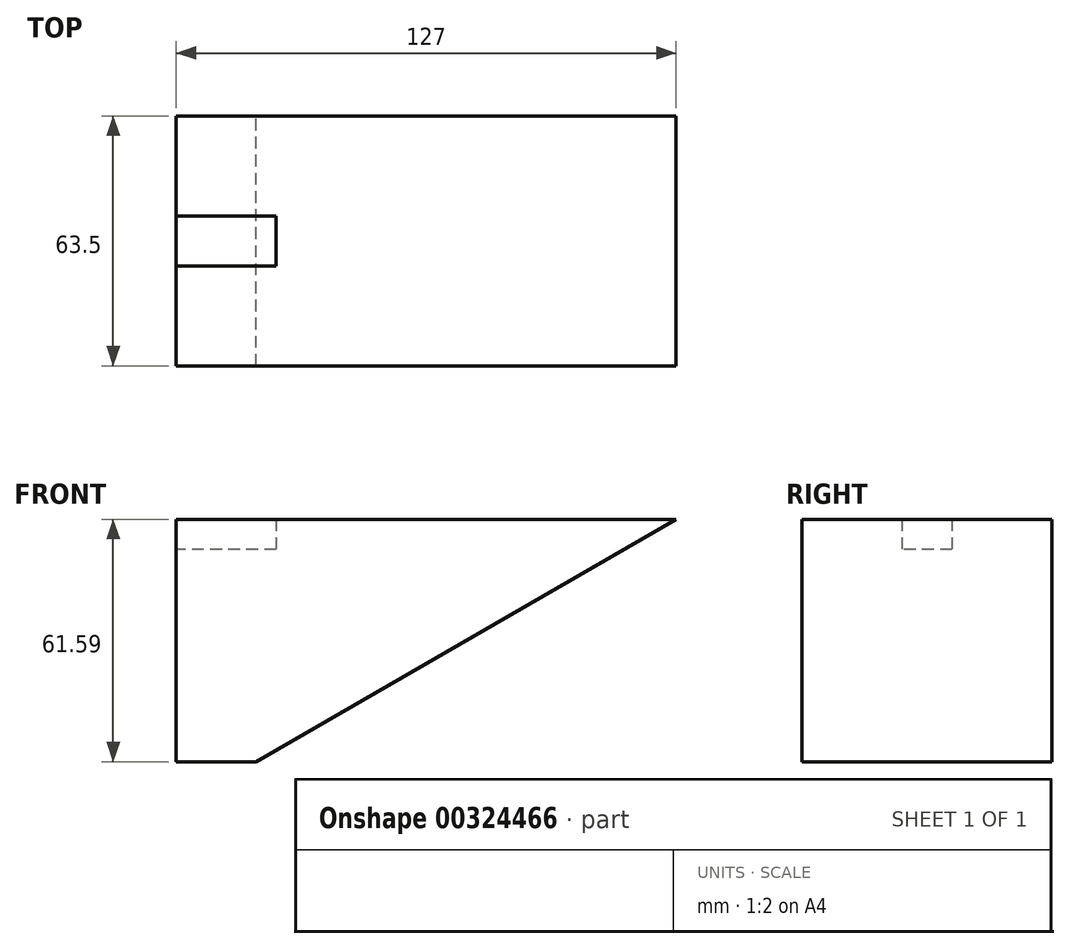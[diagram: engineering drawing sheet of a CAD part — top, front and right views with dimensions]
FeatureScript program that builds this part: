
annotation { "Feature Type Name" : "Feature", "Feature Type Description" : "" }
export const myFeature = defineFeature(function(context is Context, id is Id, definition is map)
    precondition{}
    {
        {
            var Q0;
            Q0=qCreatedBy(makeId("Front.planeOp"),FACE);
            var sketch = newSketch(context, id + "F0", { "sketchPlane" : qUnion([Q0])});
            skLineSegment(sketch, "E0", {"start": v(0, 0) * mm, "end": v(20.32, 0) * mm});
            skLineSegment(sketch, "E1", {"start": v(0, 0) * mm, "end": v(0, 61.6) * mm});
            skLineSegment(sketch, "E2", {"start": v(127, 61.6) * mm, "end": v(20.32, 0) * mm});
            skLineSegment(sketch, "E3", {"start": v(62.26, 61.6) * mm, "end": v(127, 61.6) * mm});
            skLineSegment(sketch, "E4", {"start": v(0, 61.6) * mm, "end": v(127, 61.6) * mm});
            skSolve(sketch);
        }
        {
            var Q0;
            Q0 = qSketchRegion(id + "F0", true);
            extrude(context, id + "F1", {"entities" : qUnion([Q0]), "depth" : 63.5 * mm});
        }
        {
            var Q0;
            Q0=makeQuery(id+"F1.opExtrude","SWEPT_FACE",FACE,{"disambiguationData":[OSD([sQuery(id+"F0.wireOp",EDGE,"E1")])]});
            var sketch = newSketch(context, id + "F2", { "sketchPlane" : qUnion([Q0])});
            skLineSegment(sketch, "E5.bottom", {"start": v(25.4, 61.6) * mm, "end": v(38.1, 61.6) * mm});
            skLineSegment(sketch, "E5.top", {"start": v(25.4, 53.97) * mm, "end": v(38.1, 53.97) * mm});
            skLineSegment(sketch, "E5.left", {"start": v(25.4, 61.6) * mm, "end": v(25.4, 53.97) * mm});
            skLineSegment(sketch, "E5.right", {"start": v(38.1, 61.6) * mm, "end": v(38.1, 53.97) * mm});
            skSolve(sketch);
        }
        {
            var Q0;
            Q0 = qSketchRegion(id + "F2", true);
            extrude(context, id + "F3", {"entities" : qUnion([Q0]), "operationType" : NewBodyOperationType.REMOVE, "oppositeDirection" : true, "depth" : 25.4 * mm});
        }
    });
